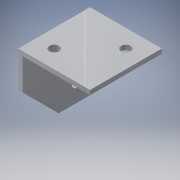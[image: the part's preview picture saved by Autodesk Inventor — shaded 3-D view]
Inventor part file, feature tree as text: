
AUTODESK INVENTOR PART (.ipt)
format: ipt  version: 2016 (Build 200138000, 138)  size: 121,344 bytes
history: native  units: in
note: dims shown in document units (in); Inventor stores cm internally (conversion verified against a paired STEP export)
features: extrude x3, sketch x3
ambient origin geometry x8: Origin, YZ Plane, XZ Plane, XY Plane, X Axis, Y Axis, Z Axis, Center Point
bodies: Solid1 (feature_tree)
feature tree (6):
  extrude  "Extrusion1"  Depth=0.125in
  sketch  "Sketch2"  dims[d2=1.875in d3=1.875in]
  extrude  "Extrusion4"  Depth=1.875in
  extrude  "Extrusion5"  Depth=0.125in
  sketch  "Sketch1"  dims[d0=2.0in d1=0.125in]
  sketch  "Sketch3"  dims[d4=2.0in d5=0.0in d13=1.5in d14=1.0in d15=0.5in d20=0.2656in d21=0.2656in d22=0.2656in d23=0.2656in d24=0.5in d25=0.5in d26=0.5in d27=0.375in d28=0.125in d29=0.0in d30=1.5in d31=0.125in d32=0.0in]
